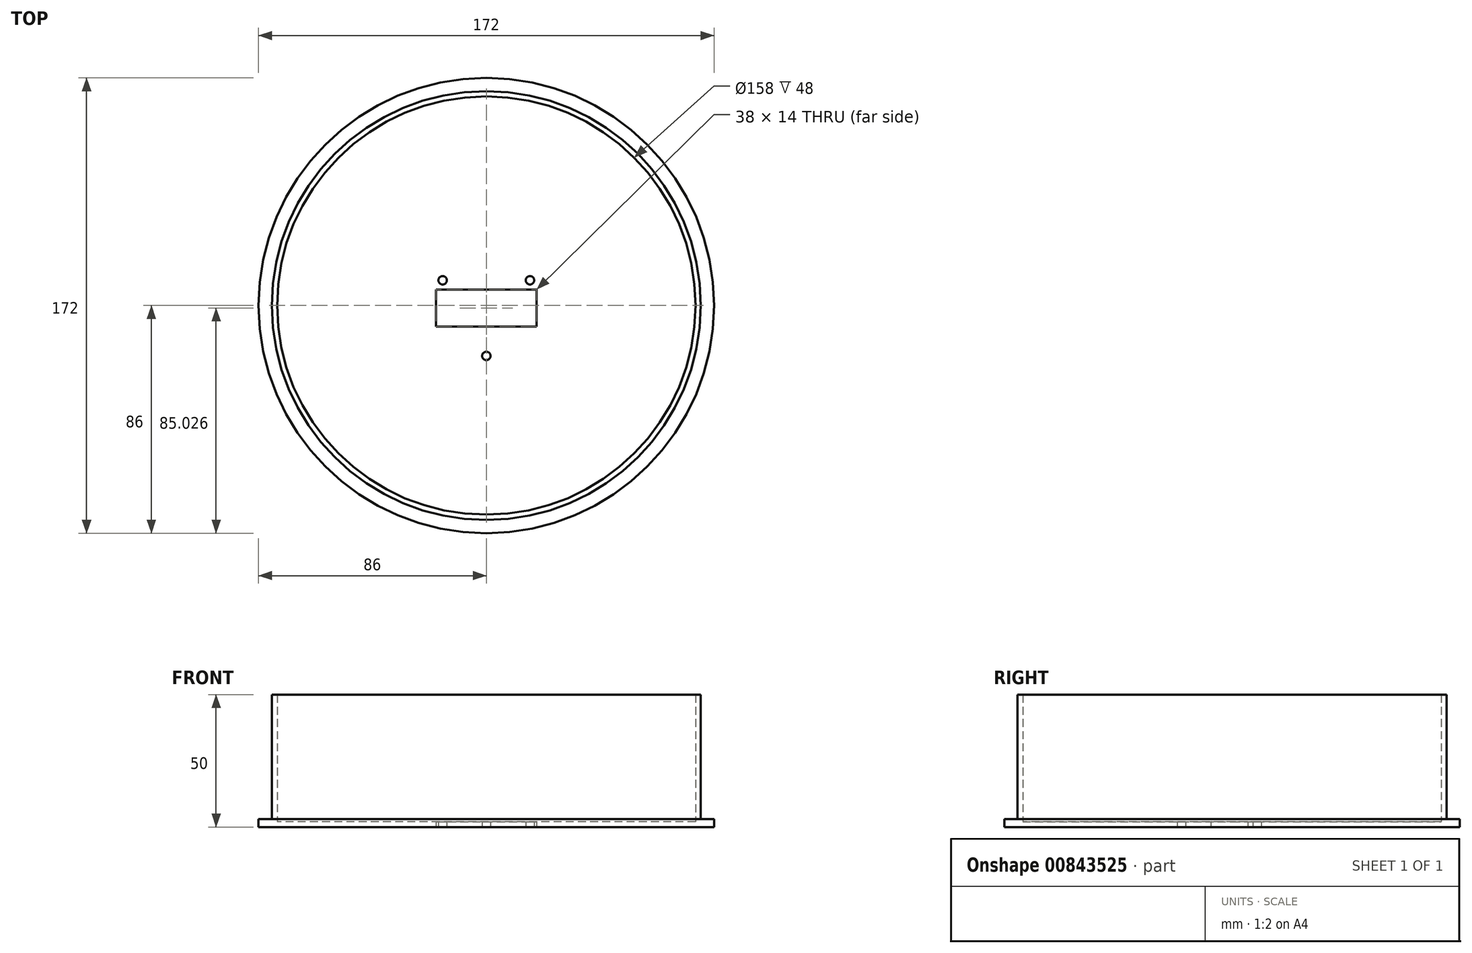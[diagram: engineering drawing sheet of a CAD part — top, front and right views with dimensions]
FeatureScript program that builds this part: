
annotation { "Feature Type Name" : "Feature", "Feature Type Description" : "" }
export const myFeature = defineFeature(function(context is Context, id is Id, definition is map)
    precondition{}
    {
        {
            var Q0;
            Q0=qCreatedBy(makeId("Top.planeOp"),FACE);
            var sketch = newSketch(context, id + "F0", { "sketchPlane" : qUnion([Q0])});
            skCircle(sketch, "E0", {"center": v(0, 0) * mm, "radius": 86 * mm});
            skCircle(sketch, "E1", {"center": v(0, 0) * mm, "radius": 81 * mm});
            skSolve(sketch);
        }
        {
            var Q0;
            Q0=makeQuery(id+"F0.imprint","IMPRINT",FACE,{"disambiguationData":[TD([[makeQuery(id+"F0.imprint","IMPRINT",EDGE,{"derivedFrom":sQuery(id+"F0.wireOp",EDGE,"E0")}),1.0]])]});
            var Q1;
            Q1=makeQuery(id+"F0.imprint","IMPRINT",FACE,{"disambiguationData":[TD([[makeQuery(id+"F0.imprint","IMPRINT",EDGE,{"derivedFrom":sQuery(id+"F0.wireOp",EDGE,"E1")}),1.0]])]});
            extrude(context, id + "F1", {"entities" : qUnion([Q0, Q1]), "depth" : 3 * mm, "offsetDistance" : 25 * mm});
        }
        {
            var Q0;
            Q0=makeQuery(id+"F0.imprint","IMPRINT",FACE,{"disambiguationData":[TD([[makeQuery(id+"F0.imprint","IMPRINT",EDGE,{"derivedFrom":sQuery(id+"F0.wireOp",EDGE,"E1")}),1.0]])]});
            extrude(context, id + "F2", {"entities" : qUnion([Q0]), "operationType" : NewBodyOperationType.ADD, "depth" : 50 * mm, "offsetDistance" : 25 * mm});
        }
        {
            var Q0;
            Q0=makeQuery(id+"F2.opExtrude","CAP_FACE",FACE,{"disambiguationData":[OSD([sQuery(id+"F0.wireOp",EDGE,"E1")])],"isStart":false});
            shell(context, id + "F3", {"entities" : qUnion([Q0]), "thickness" : 2 * mm});
        }
        {
            var Q0;
            Q0=makeQuery(id+"F1.opExtrude","CAP_FACE",FACE,{"disambiguationData":[OSD([sQuery(id+"F0.wireOp",EDGE,"E0")])],"isStart":true});
            var sketch = newSketch(context, id + "F4", { "sketchPlane" : qUnion([Q0])});
            skPoint(sketch, "E2.0.midPoint", {"position": v(8.25, 4.76) * mm});
            skCircle(sketch, "E3", {"center": v(0, 19.05) * mm, "radius": 1.6 * mm});
            skCircle(sketch, "E4", {"center": v(-16.5, -9.53) * mm, "radius": 1.6 * mm});
            skCircle(sketch, "E5", {"center": v(16.5, -9.53) * mm, "radius": 1.6 * mm});
            skLineSegment(sketch, "E6.bottom", {"start": v(-19, -6.03) * mm, "end": v(19, -6.03) * mm});
            skLineSegment(sketch, "E6.top", {"start": v(-19, 7.97) * mm, "end": v(19, 7.97) * mm});
            skLineSegment(sketch, "E6.left", {"start": v(-19, -6.03) * mm, "end": v(-19, 7.97) * mm});
            skLineSegment(sketch, "E6.right", {"start": v(19, -6.03) * mm, "end": v(19, 7.97) * mm});
            skSolve(sketch);
        }
        {
            var Q0;
            Q0=makeQuery(id+"F4.imprint","IMPRINT",FACE,{"disambiguationData":[TD([[makeQuery(id+"F4.imprint","IMPRINT",EDGE,{"derivedFrom":sQuery(id+"F4.wireOp",EDGE,"E3")}),1.0]])]});
            var Q1;
            Q1=makeQuery(id+"F4.imprint","IMPRINT",FACE,{"disambiguationData":[TD([[makeQuery(id+"F4.imprint","IMPRINT",EDGE,{"derivedFrom":sQuery(id+"F4.wireOp",EDGE,"E6.bottom")}),1.0]])]});
            var Q2;
            Q2=makeQuery(id+"F4.imprint","IMPRINT",FACE,{"disambiguationData":[TD([[makeQuery(id+"F4.imprint","IMPRINT",EDGE,{"derivedFrom":sQuery(id+"F4.wireOp",EDGE,"E5")}),1.0]])]});
            var Q3;
            Q3=makeQuery(id+"F4.imprint","IMPRINT",FACE,{"disambiguationData":[TD([[makeQuery(id+"F4.imprint","IMPRINT",EDGE,{"derivedFrom":sQuery(id+"F4.wireOp",EDGE,"E4")}),1.0]])]});
            extrude(context, id + "F5", {"entities" : qUnion([Q0, Q1, Q2, Q3]), "operationType" : NewBodyOperationType.REMOVE, "oppositeDirection" : true, "depth" : 2 * mm, "offsetDistance" : 25 * mm});
        }
    });
